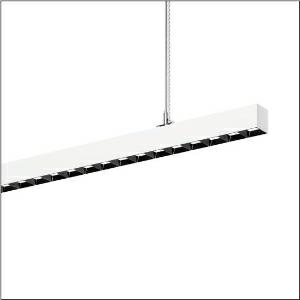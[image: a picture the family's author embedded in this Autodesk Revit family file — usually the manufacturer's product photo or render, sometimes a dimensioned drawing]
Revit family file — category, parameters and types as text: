
# Revit family: silica_21_51mx31dc3dwb
name_source: partatom
category: Lighting Fixtures
units: mm (PartAtom-declared; Revit-internal decimal feet)

## family parameters
Cut with Voids When Loaded = No
Host = Face
Light Source = No
Part Type = Normal
Room Calculation Point = No
Round Connector Dimension = Use Diameter
Shared = No

## types (1)
- --- (1 x LED, 18230 lm, 113.3 W, 3000K)
    Apparent Load = 113 VA
    CIE Flux Codes = 87 99 100 59 100
    Color Rendering = 80
    Color Temperature = 3000K
    Default Elevation = 1800 mm
    Description = Silica 21, office luminaire, primary light control with darklight reflector, of PMMA, black, CAT 2 (L<= 3000cd/m²), light emission: direct/indirect distribution, primary light characteristic: symmetric, installation type: suspended mounting, LED, rated luminous flux: 18.230lm, luminous efficacy: 161lm/W, light colour: 830, colour temperature: 3000K, control gear: DALI 2, with terminal, 3+2-pole, max. 2.5mm², mains connection: 220..240V, AC, 50/60Hz, rated input power: 113.3W, luminaire housing, of aluminium, traffic white (RAL 9016), length: 3.004mm, width: 53mm, height: 53mm, protection rating (complete): IP20, insulation class (complete): insulation class I (protective earthing), certification: CE, permissible operating ambient temperature: 0..+35°C, standard: EN 50419, packaging unit: 1 piece
    Height = 53 mm
    Lamp = 1 x LED
    Lamp Light Flux = 18230 lm
    Lamp Power = 113.3 W
    Lamp count = 1
    Length = 3004 mm
    Luminous efficacy = 161 lm/W
    Manufacturer = Siteco
    ModVariant = No
    Model = 51MX31DC3DWB
    Mounting Place = Ceiling
    Mounting Type = Pendant
    Number of Poles = 1
    OnlyDefault = Yes
    Power Factor = 1
    Product Name = Silica 21
    Product group = office luminaire | ceiling pendant
    ProductGroupID = 903
    Protection Class = Protection class I
    Protection Degree = IP 20
    RLX_Detail_Level = 1
    RLX_Emergency_Light_Flux = 0 lm
    RLX_Emergency_Type = 0
    RLX_Emergency_Type_DB = No
    RlxData = <blob elided: 64305 chars, md5=7f464c4f>
    Socket = socket
    Standby Power = 0 W
    System Light Flux = 18230 lm
    System Power = 113 W
    Type Comments = factory setting: luminous flux: 100 % | dim-lin: 254 | 392 mA
    Type Image = l_1335871.jpg
    URL = http://relux.com
    VarID = @adj_121353
    Voltage = 0 V
    Weight = 0.00 kg
    Width = 53 mm

## geometry (parser evidence)
native form markers: Blend x4, Sweep x12
no freeform markers — native parametric forms only
